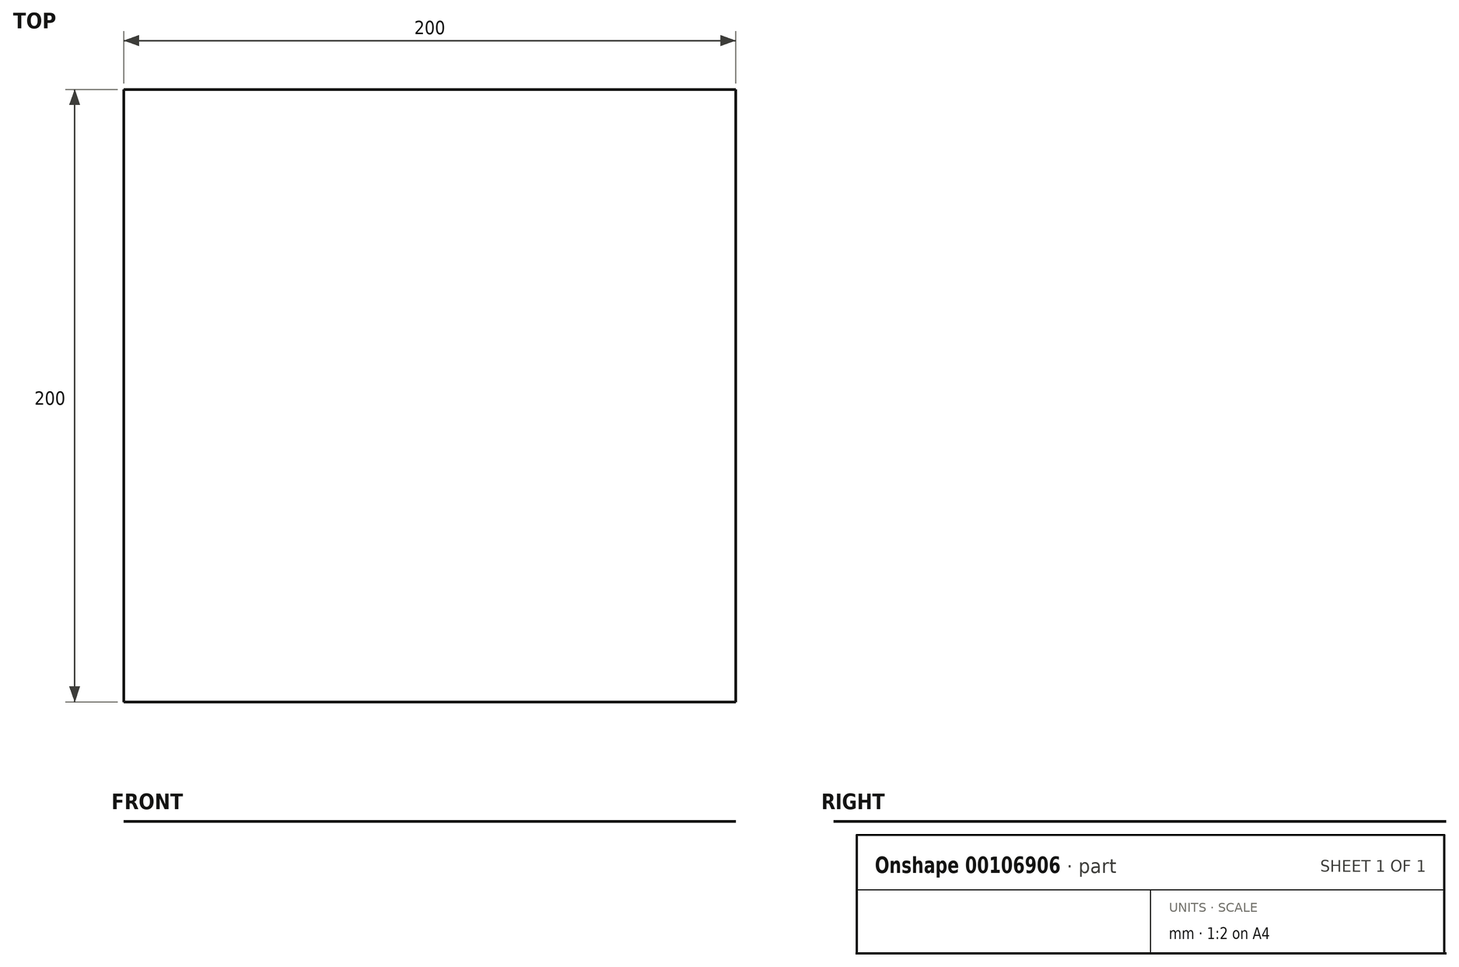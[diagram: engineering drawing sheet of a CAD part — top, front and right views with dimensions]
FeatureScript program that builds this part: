
annotation { "Feature Type Name" : "Feature", "Feature Type Description" : "" }
export const myFeature = defineFeature(function(context is Context, id is Id, definition is map)
    precondition{}
    {
        {
            var Q0;
            Q0=qCreatedBy(makeId("Top.planeOp"),FACE);
            var sketch = newSketch(context, id + "F0", { "sketchPlane" : qUnion([Q0])});
            skLineSegment(sketch, "E0.bottom", {"start": v(100, -100) * mm, "end": v(-100, -100) * mm});
            skLineSegment(sketch, "E0.top", {"start": v(100, 100) * mm, "end": v(-100, 100) * mm});
            skLineSegment(sketch, "E0.left", {"start": v(100, -100) * mm, "end": v(100, 100) * mm});
            skLineSegment(sketch, "E0.right", {"start": v(-100, -100) * mm, "end": v(-100, 100) * mm});
            skPoint(sketch, "E0.middle", {"position": v(0, 0) * mm});
            skLineSegment(sketch, "E1.bottom", {"start": v(-100, 100) * mm, "end": v(100, 100) * mm, "construction": true});
            skLineSegment(sketch, "E1.top", {"start": v(-100, 300) * mm, "end": v(100, 300) * mm, "construction": true});
            skLineSegment(sketch, "E1.left", {"start": v(-100, 100) * mm, "end": v(-100, 300) * mm, "construction": true});
            skLineSegment(sketch, "E1.right", {"start": v(100, 100) * mm, "end": v(100, 300) * mm, "construction": true});
            skLineSegment(sketch, "E2.0", {"start": v(200, -120) * mm, "end": v(200, 320) * mm, "construction": true});
            skLineSegment(sketch, "E3.0", {"start": v(-200, -120) * mm, "end": v(-200, 320) * mm, "construction": true});
            skLineSegment(sketch, "E4.0", {"start": v(-200, 320) * mm, "end": v(200, 320) * mm, "construction": true});
            skLineSegment(sketch, "E5.0", {"start": v(-200, -120) * mm, "end": v(200, -120) * mm, "construction": true});
            skLineSegment(sketch, "E6.0", {"start": v(-220, 340) * mm, "end": v(220, 340) * mm, "construction": true});
            skLineSegment(sketch, "E6.1", {"start": v(-220, -140) * mm, "end": v(-220, 340) * mm, "construction": true});
            skLineSegment(sketch, "E6.2", {"start": v(-220, -140) * mm, "end": v(220, -140) * mm, "construction": true});
            skLineSegment(sketch, "E6.3", {"start": v(220, -140) * mm, "end": v(220, 340) * mm, "construction": true});
            skSolve(sketch);
        }
        {
            var Q0;
            Q0=makeQuery(id+"F0.imprint","IMPRINT",FACE,{"disambiguationData":[TD([[makeQuery(id+"F0.imprint","IMPRINT",EDGE,{"derivedFrom":sQuery(id+"F0.wireOp",EDGE,"E0.bottom")}),-1.0]])]});
            extrude(context, id + "F1", {"entities" : qUnion([Q0]), "depth" : 1 / 203.2 * mm});
        }
    });
